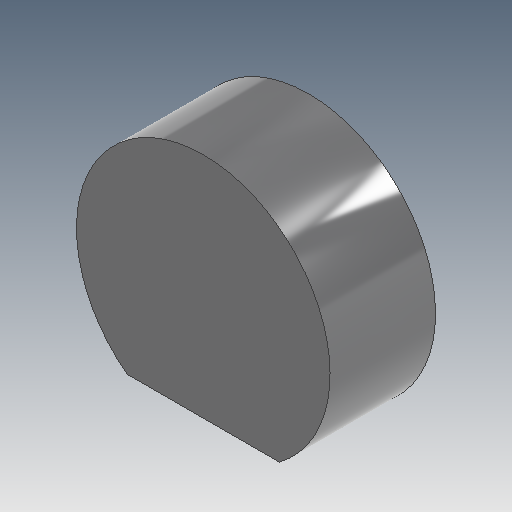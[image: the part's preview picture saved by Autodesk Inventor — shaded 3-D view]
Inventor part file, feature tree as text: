
AUTODESK INVENTOR PART (.ipt)
format: ipt  version: 2020.3 (Build 243373010, 373A)  size: 104,448 bytes
history: native  units: mm
features: extrude x1, sketch x1
ambient origin geometry x8: Origin, YZ Plane, XZ Plane, XY Plane, X Axis, Y Axis, Z Axis, Center Point
bodies: Solid1 (feature_tree)
feature tree (2):
  extrude  "Extrusion1"  Depth=12.475mm
  sketch  "Sketch1"  dims[d0=30.0mm d1=12.0mm d2=12.475mm d3=0.0mm]
